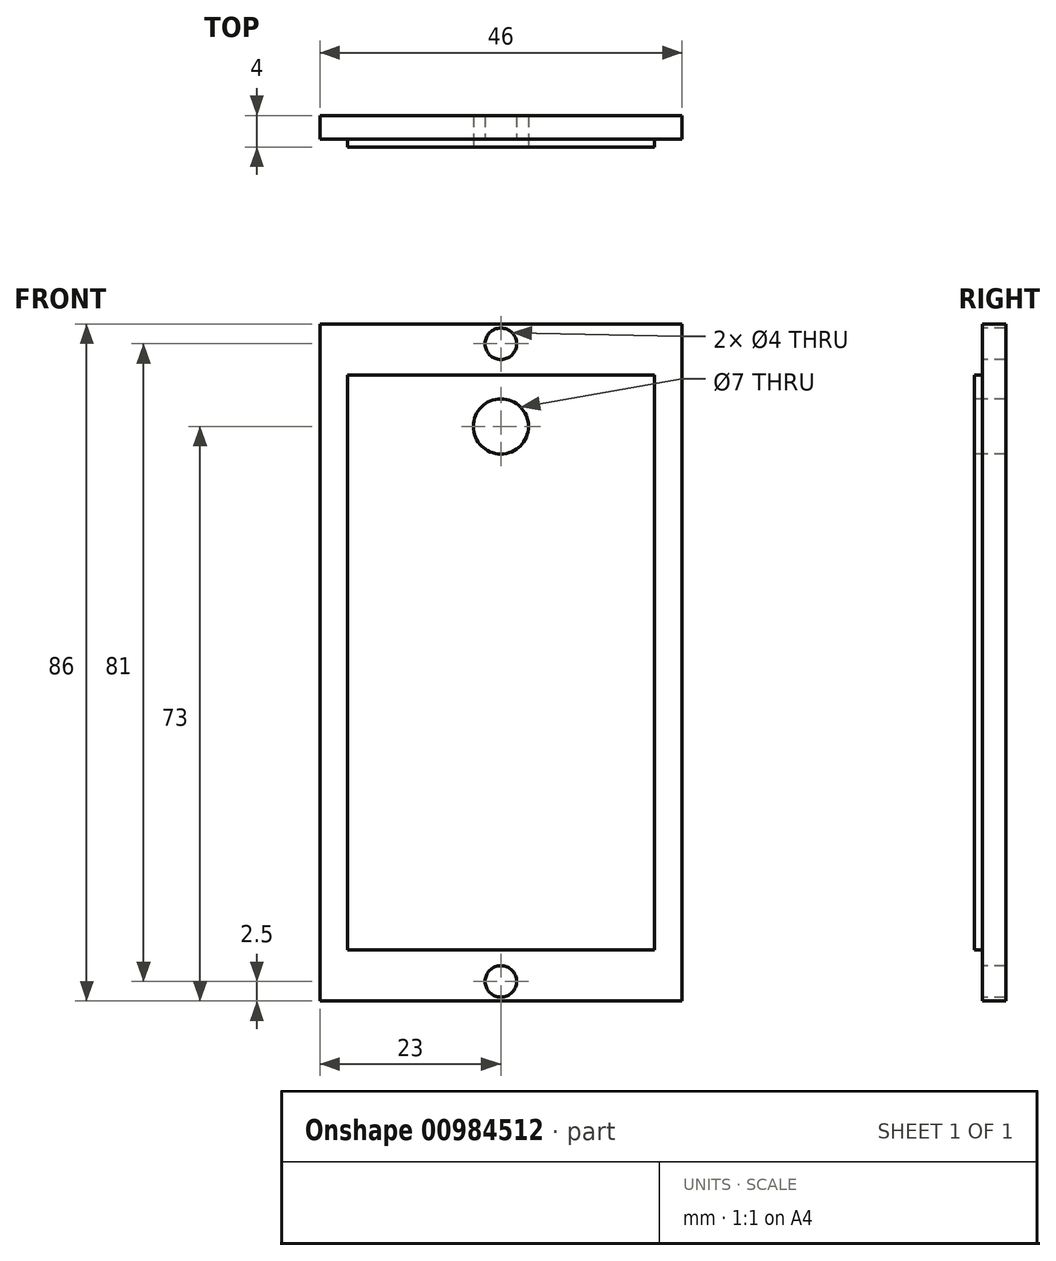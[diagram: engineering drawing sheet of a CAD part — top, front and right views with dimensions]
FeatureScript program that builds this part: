
annotation { "Feature Type Name" : "Feature", "Feature Type Description" : "" }
export const myFeature = defineFeature(function(context is Context, id is Id, definition is map)
    precondition{}
    {
        {
            var Q0;
            Q0=qCreatedBy(makeId("Front.planeOp"),FACE);
            var sketch = newSketch(context, id + "F0", { "sketchPlane" : qUnion([Q0])});
            skLineSegment(sketch, "E0.bottom", {"start": v(-23, 43) * mm, "end": v(23, 43) * mm});
            skLineSegment(sketch, "E0.top", {"start": v(-23, -43) * mm, "end": v(23, -43) * mm});
            skLineSegment(sketch, "E0.left", {"start": v(-23, 43) * mm, "end": v(-23, -43) * mm});
            skLineSegment(sketch, "E0.right", {"start": v(23, 43) * mm, "end": v(23, -43) * mm});
            skSolve(sketch);
        }
        {
            var Q0;
            Q0 = qSketchRegion(id + "F0", true);
            extrude(context, id + "F1", {"entities" : qUnion([Q0]), "depth" : 3 * mm, "offsetDistance" : 25 * mm});
        }
        {
            var Q0;
            Q0=makeQuery(id+"F1.opExtrude","CAP_FACE",FACE,{"disambiguationData":[OSD([sQuery(id+"F0.wireOp",EDGE,"E0.bottom"),sQuery(id+"F0.wireOp",EDGE,"E0.top"),sQuery(id+"F0.wireOp",EDGE,"E0.left"),sQuery(id+"F0.wireOp",EDGE,"E0.right")])],"isStart":false});
            var sketch = newSketch(context, id + "F2", { "sketchPlane" : qUnion([Q0])});
            skLineSegment(sketch, "E1.bottom", {"start": v(-19.5, 36.5) * mm, "end": v(19.5, 36.5) * mm});
            skLineSegment(sketch, "E1.top", {"start": v(-19.5, -36.5) * mm, "end": v(19.5, -36.5) * mm});
            skLineSegment(sketch, "E1.left", {"start": v(-19.5, 36.5) * mm, "end": v(-19.5, -36.5) * mm});
            skLineSegment(sketch, "E1.right", {"start": v(19.5, 36.5) * mm, "end": v(19.5, -36.5) * mm});
            skSolve(sketch);
        }
        {
            var Q0;
            Q0 = qSketchRegion(id + "F2", true);
            extrude(context, id + "F3", {"entities" : qUnion([Q0]), "operationType" : NewBodyOperationType.ADD, "depth" : 1 * mm, "offsetDistance" : 25 * mm});
        }
        {
            var Q0;
            Q0=makeQuery(id+"F1.opExtrude","CAP_FACE",FACE,{"disambiguationData":[OSD([sQuery(id+"F0.wireOp",EDGE,"E0.bottom"),sQuery(id+"F0.wireOp",EDGE,"E0.top"),sQuery(id+"F0.wireOp",EDGE,"E0.left"),sQuery(id+"F0.wireOp",EDGE,"E0.right")])],"isStart":false});
            var sketch = newSketch(context, id + "F4", { "sketchPlane" : qUnion([Q0])});
            skCircle(sketch, "E2", {"center": v(0, 40.5) * mm, "radius": 2 * mm});
            skCircle(sketch, "E3.MirrorC", {"center": v(0, -40.5) * mm, "radius": 2 * mm});
            skSolve(sketch);
        }
        {
            var Q0;
            Q0 = qSketchRegion(id + "F4", true);
            extrude(context, id + "F5", {"entities" : qUnion([Q0]), "operationType" : NewBodyOperationType.REMOVE, "oppositeDirection" : true, "depth" : 3 * mm, "offsetDistance" : 25 * mm});
        }
        {
            var Q0;
            Q0=makeQuery(id+"F3.opExtrude","CAP_FACE",FACE,{"disambiguationData":[OSD([sQuery(id+"F2.wireOp",EDGE,"E1.bottom"),sQuery(id+"F2.wireOp",EDGE,"E1.top"),sQuery(id+"F2.wireOp",EDGE,"E1.left"),sQuery(id+"F2.wireOp",EDGE,"E1.right")])],"isStart":false});
            var sketch = newSketch(context, id + "F6", { "sketchPlane" : qUnion([Q0])});
            skCircle(sketch, "E4", {"center": v(0, 30) * mm, "radius": 3.5 * mm});
            skSolve(sketch);
        }
        {
            var Q0;
            Q0 = qSketchRegion(id + "F6", true);
            extrude(context, id + "F7", {"entities" : qUnion([Q0]), "operationType" : NewBodyOperationType.REMOVE, "oppositeDirection" : true, "depth" : 4 * mm, "offsetDistance" : 25 * mm});
        }
    });
